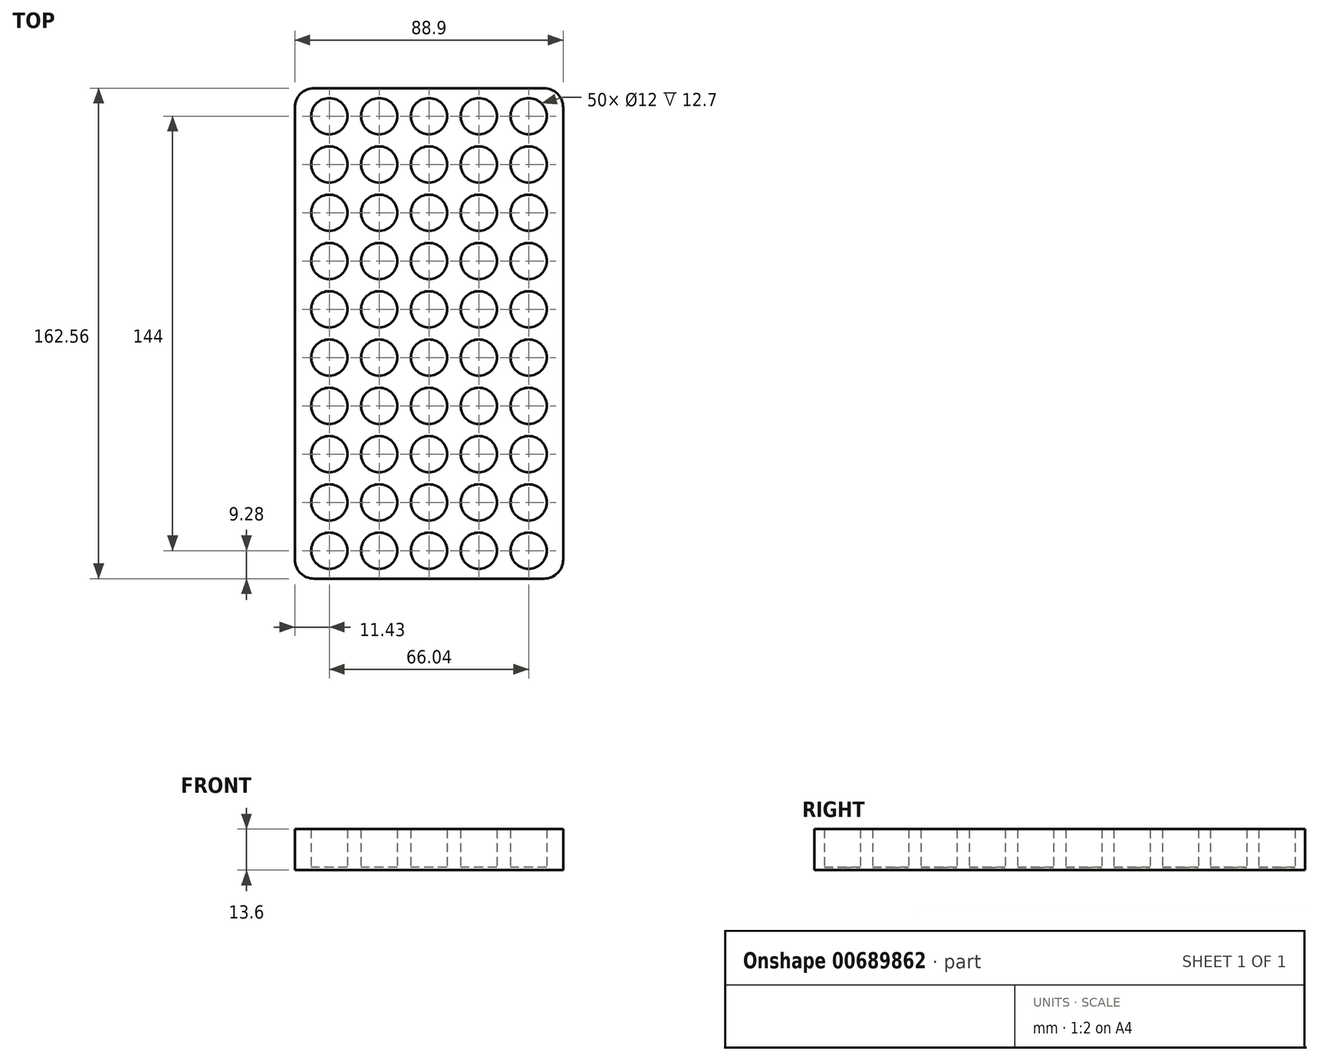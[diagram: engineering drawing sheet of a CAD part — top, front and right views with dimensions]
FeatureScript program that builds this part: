
annotation { "Feature Type Name" : "Feature", "Feature Type Description" : "" }
export const myFeature = defineFeature(function(context is Context, id is Id, definition is map)
    precondition{}
    {
        {
            var Q0;
            Q0=qCreatedBy(makeId("Top.planeOp"),FACE);
            var sketch = newSketch(context, id + "F0", { "sketchPlane" : qUnion([Q0])});
            skLineSegment(sketch, "E0.bottom", {"start": v(-38.1, 81.28) * mm, "end": v(38.1, 81.28) * mm});
            skLineSegment(sketch, "E0.top", {"start": v(-38.1, -81.28) * mm, "end": v(38.1, -81.28) * mm});
            skLineSegment(sketch, "E0.left", {"start": v(-44.45, 74.93) * mm, "end": v(-44.45, -74.93) * mm});
            skLineSegment(sketch, "E0.right", {"start": v(44.45, 74.93) * mm, "end": v(44.45, -74.93) * mm});
            skPoint(sketch, "E0.middle", {"position": v(0, 0) * mm});
            skCircle(sketch, "E1", {"center": v(-33.02, 72) * mm, "radius": 6 * mm});
            skCircle(sketch, "E2.0.1.0", {"center": v(-33.02, 56) * mm, "radius": 6 * mm});
            skCircle(sketch, "E2.0.2.0", {"center": v(-33.02, 40) * mm, "radius": 6 * mm});
            skCircle(sketch, "E2.0.3.0", {"center": v(-33.02, 24) * mm, "radius": 6 * mm});
            skCircle(sketch, "E2.0.4.0", {"center": v(-33.02, 8) * mm, "radius": 6 * mm});
            skCircle(sketch, "E2.0.5.0", {"center": v(-33.02, -8) * mm, "radius": 6 * mm});
            skCircle(sketch, "E2.0.6.0", {"center": v(-33.02, -24) * mm, "radius": 6 * mm});
            skCircle(sketch, "E2.0.7.0", {"center": v(-33.02, -40) * mm, "radius": 6 * mm});
            skCircle(sketch, "E2.0.8.0", {"center": v(-33.02, -56) * mm, "radius": 6 * mm});
            skCircle(sketch, "E2.0.9.0", {"center": v(-33.02, -72) * mm, "radius": 6 * mm});
            skCircle(sketch, "E2.1.0.0", {"center": v(-16.51, 72) * mm, "radius": 6 * mm});
            skCircle(sketch, "E2.1.1.0", {"center": v(-16.51, 56) * mm, "radius": 6 * mm});
            skCircle(sketch, "E2.1.2.0", {"center": v(-16.51, 40) * mm, "radius": 6 * mm});
            skCircle(sketch, "E2.1.3.0", {"center": v(-16.51, 24) * mm, "radius": 6 * mm});
            skCircle(sketch, "E2.1.4.0", {"center": v(-16.51, 8) * mm, "radius": 6 * mm});
            skCircle(sketch, "E2.1.5.0", {"center": v(-16.51, -8) * mm, "radius": 6 * mm});
            skCircle(sketch, "E2.1.6.0", {"center": v(-16.51, -24) * mm, "radius": 6 * mm});
            skCircle(sketch, "E2.1.7.0", {"center": v(-16.51, -40) * mm, "radius": 6 * mm});
            skCircle(sketch, "E2.1.8.0", {"center": v(-16.51, -56) * mm, "radius": 6 * mm});
            skCircle(sketch, "E2.1.9.0", {"center": v(-16.51, -72) * mm, "radius": 6 * mm});
            skCircle(sketch, "E2.2.0.0", {"center": v(0, 72) * mm, "radius": 6 * mm});
            skCircle(sketch, "E2.2.1.0", {"center": v(0, 56) * mm, "radius": 6 * mm});
            skCircle(sketch, "E2.2.2.0", {"center": v(0, 40) * mm, "radius": 6 * mm});
            skCircle(sketch, "E2.2.3.0", {"center": v(0, 24) * mm, "radius": 6 * mm});
            skCircle(sketch, "E2.2.4.0", {"center": v(0, 8) * mm, "radius": 6 * mm});
            skCircle(sketch, "E2.2.5.0", {"center": v(0, -8) * mm, "radius": 6 * mm});
            skCircle(sketch, "E2.2.6.0", {"center": v(0, -24) * mm, "radius": 6 * mm});
            skCircle(sketch, "E2.2.7.0", {"center": v(0, -40) * mm, "radius": 6 * mm});
            skCircle(sketch, "E2.2.8.0", {"center": v(0, -56) * mm, "radius": 6 * mm});
            skCircle(sketch, "E2.2.9.0", {"center": v(0, -72) * mm, "radius": 6 * mm});
            skCircle(sketch, "E2.3.0.0", {"center": v(16.51, 72) * mm, "radius": 6 * mm});
            skCircle(sketch, "E2.3.1.0", {"center": v(16.51, 56) * mm, "radius": 6 * mm});
            skCircle(sketch, "E2.3.2.0", {"center": v(16.51, 40) * mm, "radius": 6 * mm});
            skCircle(sketch, "E2.3.3.0", {"center": v(16.51, 24) * mm, "radius": 6 * mm});
            skCircle(sketch, "E2.3.4.0", {"center": v(16.51, 8) * mm, "radius": 6 * mm});
            skCircle(sketch, "E2.3.5.0", {"center": v(16.51, -8) * mm, "radius": 6 * mm});
            skCircle(sketch, "E2.3.6.0", {"center": v(16.51, -24) * mm, "radius": 6 * mm});
            skCircle(sketch, "E2.3.7.0", {"center": v(16.51, -40) * mm, "radius": 6 * mm});
            skCircle(sketch, "E2.3.8.0", {"center": v(16.51, -56) * mm, "radius": 6 * mm});
            skCircle(sketch, "E2.3.9.0", {"center": v(16.51, -72) * mm, "radius": 6 * mm});
            skCircle(sketch, "E2.4.0.0", {"center": v(33.02, 72) * mm, "radius": 6 * mm});
            skCircle(sketch, "E2.4.1.0", {"center": v(33.02, 56) * mm, "radius": 6 * mm});
            skCircle(sketch, "E2.4.2.0", {"center": v(33.02, 40) * mm, "radius": 6 * mm});
            skCircle(sketch, "E2.4.3.0", {"center": v(33.02, 24) * mm, "radius": 6 * mm});
            skCircle(sketch, "E2.4.4.0", {"center": v(33.02, 8) * mm, "radius": 6 * mm});
            skCircle(sketch, "E2.4.5.0", {"center": v(33.02, -8) * mm, "radius": 6 * mm});
            skCircle(sketch, "E2.4.6.0", {"center": v(33.02, -24) * mm, "radius": 6 * mm});
            skCircle(sketch, "E2.4.7.0", {"center": v(33.02, -40) * mm, "radius": 6 * mm});
            skCircle(sketch, "E2.4.8.0", {"center": v(33.02, -56) * mm, "radius": 6 * mm});
            skCircle(sketch, "E2.4.9.0", {"center": v(33.02, -72) * mm, "radius": 6 * mm});
            skLineSegment(sketch, "E2.direction1", {"start": v(-33.02, 72) * mm, "end": v(-16.51, 72) * mm, "construction": true});
            skLineSegment(sketch, "E2.direction2", {"start": v(-33.02, 72) * mm, "end": v(-33.02, 56) * mm, "construction": true});
            skLineSegment(sketch, "E3", {"start": v(0, 8) * mm, "end": v(0, -8) * mm, "construction": true});
            skPoint(sketch, "E4.visualSharp", {"position": v(-44.45, 81.28) * mm});
            skArc(sketch, "E4.filletArc", {"start": v(-38.1, 81.28) * mm, "mid": v(-42.6, 79.42) * mm, "end": v(-44.45, 74.93) * mm});
            skPoint(sketch, "E5.visualSharp", {"position": v(44.45, 81.28) * mm});
            skArc(sketch, "E5.filletArc", {"start": v(44.45, 74.93) * mm, "mid": v(42.6, 79.42) * mm, "end": v(38.1, 81.28) * mm});
            skPoint(sketch, "E6.visualSharp", {"position": v(44.45, -81.28) * mm});
            skArc(sketch, "E6.filletArc", {"start": v(38.1, -81.28) * mm, "mid": v(42.6, -79.42) * mm, "end": v(44.45, -74.93) * mm});
            skPoint(sketch, "E7.visualSharp", {"position": v(-44.45, -81.28) * mm});
            skArc(sketch, "E7.filletArc", {"start": v(-44.45, -74.93) * mm, "mid": v(-42.6, -79.42) * mm, "end": v(-38.1, -81.28) * mm});
            skSolve(sketch);
        }
        {
            var Q0;
            Q0 = qSketchRegion(id + "F0", true);
            extrude(context, id + "F1", {"entities" : qUnion([Q0]), "depth" : 12.7 * mm, "offsetDistance" : 25.4 * mm});
        }
        {
            var Q0;
            Q0=makeQuery(id+"F1.opExtrude","CAP_FACE",FACE,{"disambiguationData":[OSD([sQuery(id+"F0.wireOp",EDGE,"E0.bottom"),sQuery(id+"F0.wireOp",EDGE,"E0.top"),sQuery(id+"F0.wireOp",EDGE,"E0.left"),sQuery(id+"F0.wireOp",EDGE,"E0.right"),sQuery(id+"F0.wireOp",EDGE,"E1"),sQuery(id+"F0.wireOp",EDGE,"E2.0.1.0"),sQuery(id+"F0.wireOp",EDGE,"E2.0.2.0"),sQuery(id+"F0.wireOp",EDGE,"E2.0.3.0"),sQuery(id+"F0.wireOp",EDGE,"E2.0.4.0"),sQuery(id+"F0.wireOp",EDGE,"E2.0.5.0"),sQuery(id+"F0.wireOp",EDGE,"E2.0.6.0"),sQuery(id+"F0.wireOp",EDGE,"E2.0.7.0"),sQuery(id+"F0.wireOp",EDGE,"E2.0.8.0"),sQuery(id+"F0.wireOp",EDGE,"E2.0.9.0"),sQuery(id+"F0.wireOp",EDGE,"E2.1.0.0"),sQuery(id+"F0.wireOp",EDGE,"E2.1.1.0"),sQuery(id+"F0.wireOp",EDGE,"E2.1.2.0"),sQuery(id+"F0.wireOp",EDGE,"E2.1.3.0"),sQuery(id+"F0.wireOp",EDGE,"E2.1.4.0"),sQuery(id+"F0.wireOp",EDGE,"E2.1.5.0"),sQuery(id+"F0.wireOp",EDGE,"E2.1.6.0"),sQuery(id+"F0.wireOp",EDGE,"E2.1.7.0"),sQuery(id+"F0.wireOp",EDGE,"E2.1.8.0"),sQuery(id+"F0.wireOp",EDGE,"E2.1.9.0"),sQuery(id+"F0.wireOp",EDGE,"E2.2.0.0"),sQuery(id+"F0.wireOp",EDGE,"E2.2.1.0"),sQuery(id+"F0.wireOp",EDGE,"E2.2.2.0"),sQuery(id+"F0.wireOp",EDGE,"E2.2.3.0"),sQuery(id+"F0.wireOp",EDGE,"E2.2.4.0"),sQuery(id+"F0.wireOp",EDGE,"E2.2.5.0"),sQuery(id+"F0.wireOp",EDGE,"E2.2.6.0"),sQuery(id+"F0.wireOp",EDGE,"E2.2.7.0"),sQuery(id+"F0.wireOp",EDGE,"E2.2.8.0"),sQuery(id+"F0.wireOp",EDGE,"E2.2.9.0"),sQuery(id+"F0.wireOp",EDGE,"E2.3.0.0"),sQuery(id+"F0.wireOp",EDGE,"E2.3.1.0"),sQuery(id+"F0.wireOp",EDGE,"E2.3.2.0"),sQuery(id+"F0.wireOp",EDGE,"E2.3.3.0"),sQuery(id+"F0.wireOp",EDGE,"E2.3.4.0"),sQuery(id+"F0.wireOp",EDGE,"E2.3.5.0"),sQuery(id+"F0.wireOp",EDGE,"E2.3.6.0"),sQuery(id+"F0.wireOp",EDGE,"E2.3.7.0"),sQuery(id+"F0.wireOp",EDGE,"E2.3.8.0"),sQuery(id+"F0.wireOp",EDGE,"E2.3.9.0"),sQuery(id+"F0.wireOp",EDGE,"E2.4.0.0"),sQuery(id+"F0.wireOp",EDGE,"E2.4.1.0"),sQuery(id+"F0.wireOp",EDGE,"E2.4.2.0"),sQuery(id+"F0.wireOp",EDGE,"E2.4.3.0"),sQuery(id+"F0.wireOp",EDGE,"E2.4.4.0"),sQuery(id+"F0.wireOp",EDGE,"E2.4.5.0"),sQuery(id+"F0.wireOp",EDGE,"E2.4.6.0"),sQuery(id+"F0.wireOp",EDGE,"E2.4.7.0"),sQuery(id+"F0.wireOp",EDGE,"E2.4.8.0"),sQuery(id+"F0.wireOp",EDGE,"E2.4.9.0"),sQuery(id+"F0.wireOp",EDGE,"E4.filletArc"),sQuery(id+"F0.wireOp",EDGE,"E5.filletArc"),sQuery(id+"F0.wireOp",EDGE,"E6.filletArc"),sQuery(id+"F0.wireOp",EDGE,"E7.filletArc")])],"isStart":true});
            var sketch = newSketch(context, id + "F2", { "sketchPlane" : qUnion([Q0])});
            skArc(sketch, "E8.0.0", {"start": v(-38.1, 81.28) * mm, "mid": v(-42.6, 79.42) * mm, "end": v(-44.45, 74.93) * mm});
            skLineSegment(sketch, "E8.0.1", {"start": v(-44.45, 74.93) * mm, "end": v(-44.45, -74.93) * mm});
            skArc(sketch, "E8.0.2", {"start": v(-44.45, -74.93) * mm, "mid": v(-42.6, -79.42) * mm, "end": v(-38.1, -81.28) * mm});
            skLineSegment(sketch, "E8.0.3", {"start": v(-38.1, -81.28) * mm, "end": v(38.1, -81.28) * mm});
            skArc(sketch, "E8.0.4", {"start": v(38.1, -81.28) * mm, "mid": v(42.6, -79.42) * mm, "end": v(44.45, -74.93) * mm});
            skLineSegment(sketch, "E8.0.5", {"start": v(44.45, -74.93) * mm, "end": v(44.45, 74.93) * mm});
            skArc(sketch, "E8.0.6", {"start": v(44.45, 74.93) * mm, "mid": v(42.6, 79.42) * mm, "end": v(38.1, 81.28) * mm});
            skLineSegment(sketch, "E8.0.7", {"start": v(38.1, 81.28) * mm, "end": v(-38.1, 81.28) * mm});
            skSolve(sketch);
        }
        {
            var Q0;
            Q0 = qSketchRegion(id + "F2", true);
            extrude(context, id + "F3", {"entities" : qUnion([Q0]), "operationType" : NewBodyOperationType.ADD, "depth" : .9 * mm, "offsetDistance" : 25.4 * mm});
        }
    });
